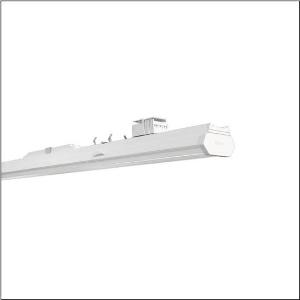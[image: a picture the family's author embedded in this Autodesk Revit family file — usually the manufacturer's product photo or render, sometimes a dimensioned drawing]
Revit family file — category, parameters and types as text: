
# Revit family: licross_r__11_protected_mo_51tp12dn59xf_cb84
name_source: partatom
category: Lighting Fixtures
units: mm (PartAtom-declared; Revit-internal decimal feet)

## family parameters
Cut with Voids When Loaded = No
Host = Face
Light Source = No
Part Type = Normal
Room Calculation Point = No
Round Connector Dimension = Use Diameter
Shared = No

## types (1)
- --- (1 x LED, 9030 lm, 56.2 W, 5000K)
    Apparent Load = 56 VA
    CIE Flux Codes = 73 92 98 99 100
    Color Rendering = 80
    Color Temperature = 5000K
    Default Elevation = 1800 mm
    Description = Licross® 11 Protected MO, luminaire insert, of sheet steel, galvanised, coil coated, white, length: 1.500mm, width: 90mm, height: 101mm, LED rated luminous flux: 9.030lm, light colour: 850, control gear: DALI 2, control gear: ECG DALI, with plug, 5-pole, with phase selection, mains connection: 220..240V, AC, 50/60Hz, rated input power: 56W, halogen-free wiring, primary optical cover: cover, of PMMA, light emission: direct distribution, primary light characteristic: symmetric, protection rating (complete): IP64, insulation class (complete): insulation class I (protective earthing), certification: CE, ENEC, VDE, UKCA, protection symbol: D if used in an environment with conductive dust loads with corresponding accessories, impact resistance: IK06, permissible ambient temperature for indoor applications: -25..+40°C, reducing of maximum allowable ambient temperature of 5°C with ceiling mounting, corresponds to IFS (International Featured Standards) requirements for safety and quality in the food industry, LABS conformity tested according to VDMA 24364:2018-05, packaging unit: 1 piece
    Height = 92 mm
    Lamp = 1 x LED
    Lamp Light Flux = 9030 lm
    Lamp Power = 56.2 W
    Lamp count = 1
    Length = 1500 mm
    Luminous efficacy = 161 lm/W
    Manufacturer = Siteco
    ModVariant = No
    Model = 51TP12DN59XF
    Mounting Place = Ceiling
    Mounting Type = Pendant
    Number of Poles = 1
    OnlyDefault = Yes
    Power Factor = 1
    Product Name = Licross® 11 Protected MO
    Product group = luminaire insert
    ProductGroupID = 901
    Protection Class = Protection class I
    Protection Degree = IP 64
    RLX_Detail_Level = 1
    RLX_Emergency_Light_Flux = 0 lm
    RLX_Emergency_Type = 0
    RLX_Emergency_Type_DB = No
    RlxData = <blob elided: 24153 chars, md5=e748bef2>
    Socket = socket
    Standby Power = 0 W
    System Light Flux = 9030 lm
    System Power = 56 W
    Type Comments = factory setting: luminous flux: 100 % | dim-lin: 254 | 370 mA
    Type Image = l_1256148.jpg
    URL = http://relux.com
    VarID = @adj_143557
    Voltage = 0 V
    Weight = 0.00 kg
    Width = 88 mm

## geometry (parser evidence)
native form markers: Blend x4, Sweep x12
no freeform markers — native parametric forms only
